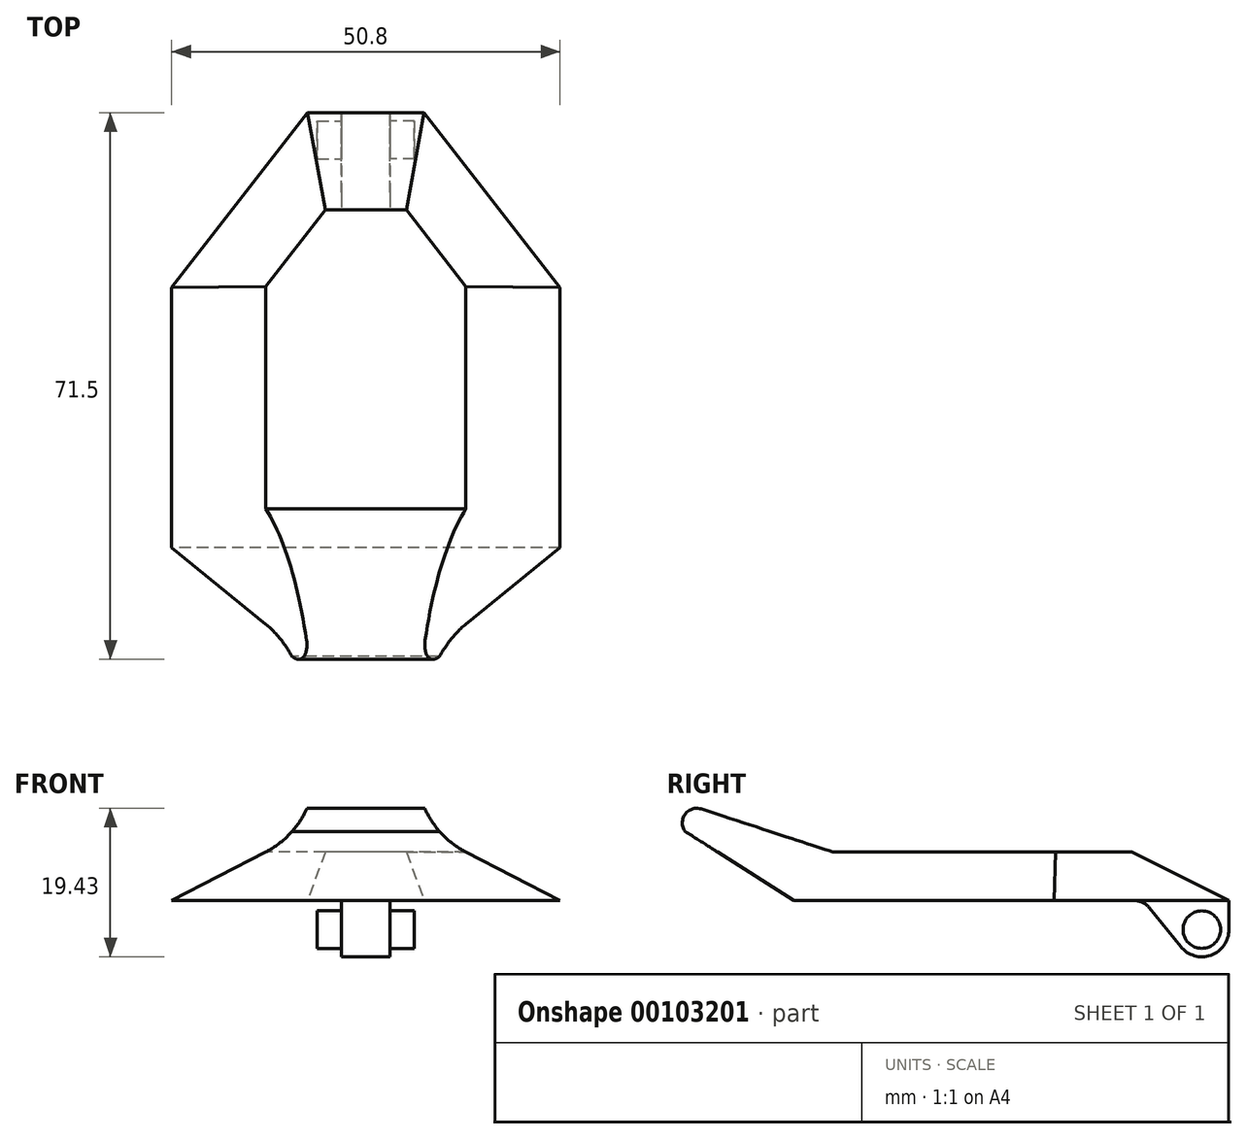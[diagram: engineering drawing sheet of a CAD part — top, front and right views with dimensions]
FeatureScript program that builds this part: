
annotation { "Feature Type Name" : "Feature", "Feature Type Description" : "" }
export const myFeature = defineFeature(function(context is Context, id is Id, definition is map)
    precondition{}
    {
        {
            var Q0;
            Q0=qCreatedBy(makeId("Right.planeOp"),FACE);
            var sketch = newSketch(context, id + "F0", { "sketchPlane" : qUnion([Q0])});
            skCircle(sketch, "E0", {"center": v(0, 0) * mm, "radius": 2.45 * mm});
            skCircle(sketch, "E1", {"center": v(0, 0) * mm, "radius": 3.56 * mm});
            skLineSegment(sketch, "E2", {"start": v(-48.26, 10.16) * mm, "end": v(-9.14, 10.16) * mm});
            skLineSegment(sketch, "E3.0", {"start": v(-53.34, 3.8) * mm, "end": v(-8.84, 3.8) * mm});
            skArc(sketch, "E4", {"start": v(-65.45, 15.78) * mm, "mid": v(-67.58, 15.09) * mm, "end": v(-67.58, 12.84) * mm});
            skLineSegment(sketch, "E5", {"start": v(-6.86, 2.86) * mm, "end": v(-2.77, -2.23) * mm});
            skPoint(sketch, "E6.visualSharp", {"position": v(-7.62, 3.8) * mm});
            skArc(sketch, "E6.filletArc", {"start": v(-6.86, 2.86) * mm, "mid": v(-7.74, 3.56) * mm, "end": v(-8.84, 3.8) * mm});
            skLineSegment(sketch, "E7", {"start": v(3.56, 0) * mm, "end": v(3.56, 3.81) * mm});
            skLineSegment(sketch, "E8", {"start": v(3.56, 3.81) * mm, "end": v(-9.14, 10.16) * mm});
            skLineSegment(sketch, "E9", {"start": v(-67.58, 12.84) * mm, "end": v(-53.34, 3.8) * mm});
            skLineSegment(sketch, "E10", {"start": v(-48.26, 10.16) * mm, "end": v(-65.45, 15.78) * mm});
            skSolve(sketch);
        }
        {
            var Q0;
            Q0=makeQuery(id+"F0.imprint","IMPRINT",FACE,{"disambiguationData":[TD([[makeQuery(id+"F0.imprint","IMPRINT",EDGE,{"derivedFrom":sQuery(id+"F0.wireOp",EDGE,"E0")}),1.0]])]});
            extrude(context, id + "F1", {"entities" : qUnion([Q0]), "depth" : 6.35 * mm});
        }
        {
            var Q0;
            Q0 = qSketchRegion(id + "F0", true);
            extrude(context, id + "F2", {"entities" : qUnion([Q0]), "operationType" : NewBodyOperationType.ADD, "depth" : 3.17 * mm});
        }
        {
            var Q0;
            Q0=makeQuery(id+"F2.opExtrude","CAP_FACE",FACE,{"disambiguationData":[OSD([sQuery(id+"F0.wireOp",EDGE,"E0"),sQuery(id+"F0.wireOp",EDGE,"E1"),sQuery(id+"F0.wireOp",EDGE,"E2"),sQuery(id+"F0.wireOp",EDGE,"0e792da8-4793-4587-a3b8-13d6d6275e47"),sQuery(id+"F0.wireOp",EDGE,"E3.0"),sQuery(id+"F0.wireOp",EDGE,"E3.1"),sQuery(id+"F0.wireOp",EDGE,"E4"),sQuery(id+"F0.wireOp",EDGE,"E5"),sQuery(id+"F0.wireOp",EDGE,"E6.filletArc"),sQuery(id+"F0.wireOp",EDGE,"E7"),sQuery(id+"F0.wireOp",EDGE,"E8")])],"isStart":false});
            var sketch = newSketch(context, id + "F3", { "sketchPlane" : qUnion([Q0])});
            skLineSegment(sketch, "E11", {"start": v(3.56, 3.81) * mm, "end": v(-8.84, 3.8) * mm});
            skSolve(sketch);
        }
        {
            var Q0;
            Q0=makeQuery(id+"F3.imprint","IMPRINT",FACE,{"disambiguationData":[TD([[makeQuery(id+"F3.imprint","IMPRINT",EDGE,{"derivedFrom":sQuery(id+"F3.wireOp",EDGE,"E11")}),-1.0]])]});
            extrude(context, id + "F4", {"entities" : qUnion([Q0]), "operationType" : NewBodyOperationType.ADD, "depth" : 22.22 * mm});
        }
        {
            var Q0;
            Q0=qCreatedBy(makeId("Right.planeOp"),FACE);
            cPlane(context, id + "F5", {"entities" : qUnion([Q0]), "cplaneType" : CPlaneType.OFFSET, "offset" : 7.62 * mm, "width" : 152.4 * mm, "height" : 152.4 * mm});
        }
        {
            var Q0;
            Q0=qCreatedBy(id+"F5.planeOp",FACE);
            var sketch = newSketch(context, id + "F6", { "sketchPlane" : qUnion([Q0])});
            skLineSegment(sketch, "E12", {"start": v(0, 0) * mm, "end": v(0, 3.81) * mm});
            skLineSegment(sketch, "E13", {"start": v(0, 3.81) * mm, "end": v(3.56, 3.81) * mm});
            skLineSegment(sketch, "E14", {"start": v(0, 0) * mm, "end": v(0, 12.98) * mm});
            skPoint(sketch, "E14.endSnap0", {"position": v(0, 1.9) * mm});
            skLineSegment(sketch, "E15", {"start": v(0, 12.98) * mm, "end": v(-60.93, 12.98) * mm});
            skSolve(sketch);
        }
        {
            var Q0;
            Q0=qCreatedBy(makeId("Front.planeOp"),FACE);
            cPlane(context, id + "F7", {"entities" : qUnion([Q0]), "cplaneType" : CPlaneType.OFFSET, "offset" : 7.62 * mm, "width" : 152.4 * mm, "height" : 152.4 * mm});
        }
        {
            var Q0;
            Q0=qCreatedBy(id+"F7.planeOp",FACE);
            var sketch = newSketch(context, id + "F8", { "sketchPlane" : qUnion([Q0])});
            skLineSegment(sketch, "E16", {"start": v(0, 0) * mm, "end": v(0, 3.8) * mm});
            skLineSegment(sketch, "E17", {"start": v(0, 3.8) * mm, "end": v(25.4, 3.8) * mm});
            skLineSegment(sketch, "E18", {"start": v(12.7, 3.8) * mm, "end": v(12.7, 7.62) * mm});
            skSolve(sketch);
        }
        {
            var Q0;
            Q0=sQuery(id+"F6.wireOp",VERTEX,"E15.end");
            var Q1;
            Q1=sQuery(id+"F6.wireOp",VERTEX,"E15.start");
            var Q2;
            Q2=sQuery(id+"F8.wireOp",VERTEX,"E17.end");
            cPlane(context, id + "F9", {"entities" : qUnion([Q0, Q1, Q2]), "cplaneType" : CPlaneType.THREE_POINT, "offset" : 152.4 * mm, "width" : 152.4 * mm, "height" : 152.4 * mm});
        }
        {
            var Q0;
            Q0=qCreatedBy(id+"F9.planeOp",FACE);
            var sketch = newSketch(context, id + "F10", { "sketchPlane" : qUnion([Q0])});
            skLineSegment(sketch, "E19.bottom", {"start": v(-12.47, -47.53) * mm, "end": v(44.27, -47.53) * mm});
            skLineSegment(sketch, "E19.top", {"start": v(-12.47, 16.28) * mm, "end": v(44.27, 16.28) * mm});
            skLineSegment(sketch, "E19.left", {"start": v(-12.47, -47.53) * mm, "end": v(-12.47, 16.28) * mm});
            skLineSegment(sketch, "E19.right", {"start": v(44.27, -47.53) * mm, "end": v(44.27, 16.28) * mm});
            skSolve(sketch);
        }
        {
            var Q0;
            Q0 = qSketchRegion(id + "F10", true);
            extrude(context, id + "F11", {"entities" : qUnion([Q0]), "operationType" : NewBodyOperationType.REMOVE, "depth" : 25.4 * mm});
        }
        {
            var Q0;
            Q0=qCreatedBy(makeId("Front.planeOp"),FACE);
            cPlane(context, id + "F12", {"entities" : qUnion([Q0]), "cplaneType" : CPlaneType.OFFSET, "offset" : 5.33 * mm, "width" : 152.4 * mm, "height" : 152.4 * mm});
        }
        {
            var Q0;
            {var subQ0=makeQuery(id+"F2.opExtrude","SWEPT_FACE",FACE,{"disambiguationData":[OSD([sQuery(id+"F0.wireOp",EDGE,"E7")])]});Q0=makeQuery(id+"FAjr1BFdUCnEszU_1.boolean.opBoolean","MERGE",FACE,{"derivedFrom":[subQ0,makeQuery(id+"FAjr1BFdUCnEszU_1.opPattern","COPY",FACE,{"derivedFrom":subQ0,"instanceName":"1"})]});}
            cPlane(context, id + "F13", {"entities" : qUnion([Q0]), "cplaneType" : CPlaneType.OFFSET, "offset" : 22.86 * mm, "oppositeDirection" : true, "width" : 152.4 * mm, "height" : 152.4 * mm});
        }
        {
            var Q0;
            Q0=qCreatedBy(id+"F13.planeOp",FACE);
            var sketch = newSketch(context, id + "F14", { "sketchPlane" : qUnion([Q0])});
            skLineSegment(sketch, "E20", {"start": v(0, 0) * mm, "end": v(0, 10.16) * mm});
            skLineSegment(sketch, "E21", {"start": v(0, 10.16) * mm, "end": v(-13.2, 10.16) * mm});
            skLineSegment(sketch, "E22", {"start": v(0, 3.8) * mm, "end": v(-25.4, 3.8) * mm});
            skSolve(sketch);
        }
        {
            var Q0;
            Q0=sQuery(id+"F14.wireOp",VERTEX,"E21.end");
            var Q1;
            Q1=sQuery(id+"F14.wireOp",VERTEX,"E22.end");
            var Q2;
            Q2=sQuery(id+"F6.wireOp",VERTEX,"E13.end");
            cPlane(context, id + "F15", {"entities" : qUnion([Q0, Q1, Q2]), "cplaneType" : CPlaneType.THREE_POINT, "offset" : 152.4 * mm, "width" : 152.4 * mm, "height" : 152.4 * mm});
        }
        {
            var Q0;
            Q0=qCreatedBy(id+"F15.planeOp",FACE);
            var sketch = newSketch(context, id + "F16", { "sketchPlane" : qUnion([Q0])});
            skLineSegment(sketch, "E23.bottom", {"start": v(-30.47, 42.03) * mm, "end": v(52.2, 42.03) * mm});
            skLineSegment(sketch, "E23.top", {"start": v(-30.47, -30.7) * mm, "end": v(52.2, -30.7) * mm});
            skLineSegment(sketch, "E23.left", {"start": v(-30.47, 42.03) * mm, "end": v(-30.47, -30.7) * mm});
            skLineSegment(sketch, "E23.right", {"start": v(52.2, 42.03) * mm, "end": v(52.2, -30.7) * mm});
            skSolve(sketch);
        }
        {
            var Q0;
            Q0 = qSketchRegion(id + "F16", true);
            extrude(context, id + "F17", {"entities" : qUnion([Q0]), "operationType" : NewBodyOperationType.REMOVE, "oppositeDirection" : true, "depth" : 25.4 * mm});
        }
        {
            var Q0;
            Q0=makeQuery(id+"F11.boolean.opBoolean","COPY",FACE,{"derivedFrom":makeQuery(id+"F11.opExtrude","SWEPT_FACE",FACE,{"disambiguationData":[OSD([sQuery(id+"F10.wireOp",EDGE,"E19.bottom")])]})});
            var sketch = newSketch(context, id + "F18", { "sketchPlane" : qUnion([Q0])});
            skArc(sketch, "E24", {"start": v(-13.09, 10.16) * mm, "mid": v(-8.8, 13.93) * mm, "end": v(-6.78, 19.28) * mm});
            skLineSegment(sketch, "E25", {"start": v(-25.4, 3.8) * mm, "end": v(-25.4, 19.49) * mm});
            skLineSegment(sketch, "E26", {"start": v(-25.4, 19.49) * mm, "end": v(-6.78, 19.28) * mm});
            skSolve(sketch);
        }
        {
            var Q0;
            Q0=makeQuery(id+"F18.imprint","IMPRINT",FACE,{"disambiguationData":[TD([[makeQuery(id+"F18.imprint","IMPRINT",EDGE,{"derivedFrom":sQuery(id+"F18.wireOp",EDGE,"E24")}),1.0]])]});
            extrude(context, id + "F19", {"entities" : qUnion([Q0]), "operationType" : NewBodyOperationType.REMOVE, "oppositeDirection" : true, "depth" : 50.8 * mm});
        }
        {
            var Q0;
            Q0=makeQuery(id+"F11.boolean.opBoolean","COPY",FACE,{"derivedFrom":makeQuery(id+"F11.opExtrude","SWEPT_FACE",FACE,{"disambiguationData":[OSD([sQuery(id+"F10.wireOp",EDGE,"E19.bottom")])]})});
            extrude(context, id + "F20", {"entities" : qUnion([Q0]), "operationType" : NewBodyOperationType.REMOVE, "oppositeDirection" : true, "depth" : 25.4 * mm});
        }
        {
            var Q0;
            Q0=makeQuery(id+"F1.opExtrude","SWEPT_BODY",BODY,{"disambiguationData":[OSD([sQuery(id+"F0.wireOp",EDGE,"E0")])]});
            var Q1;
            Q1=qCreatedBy(makeId("Right.planeOp"),FACE);
            mirror(context, id + "F21", {"operationType" : NewBodyOperationType.ADD, "entities" : qUnion([Q0]), "mirrorPlane" : qUnion([Q1])});
        }
    });
